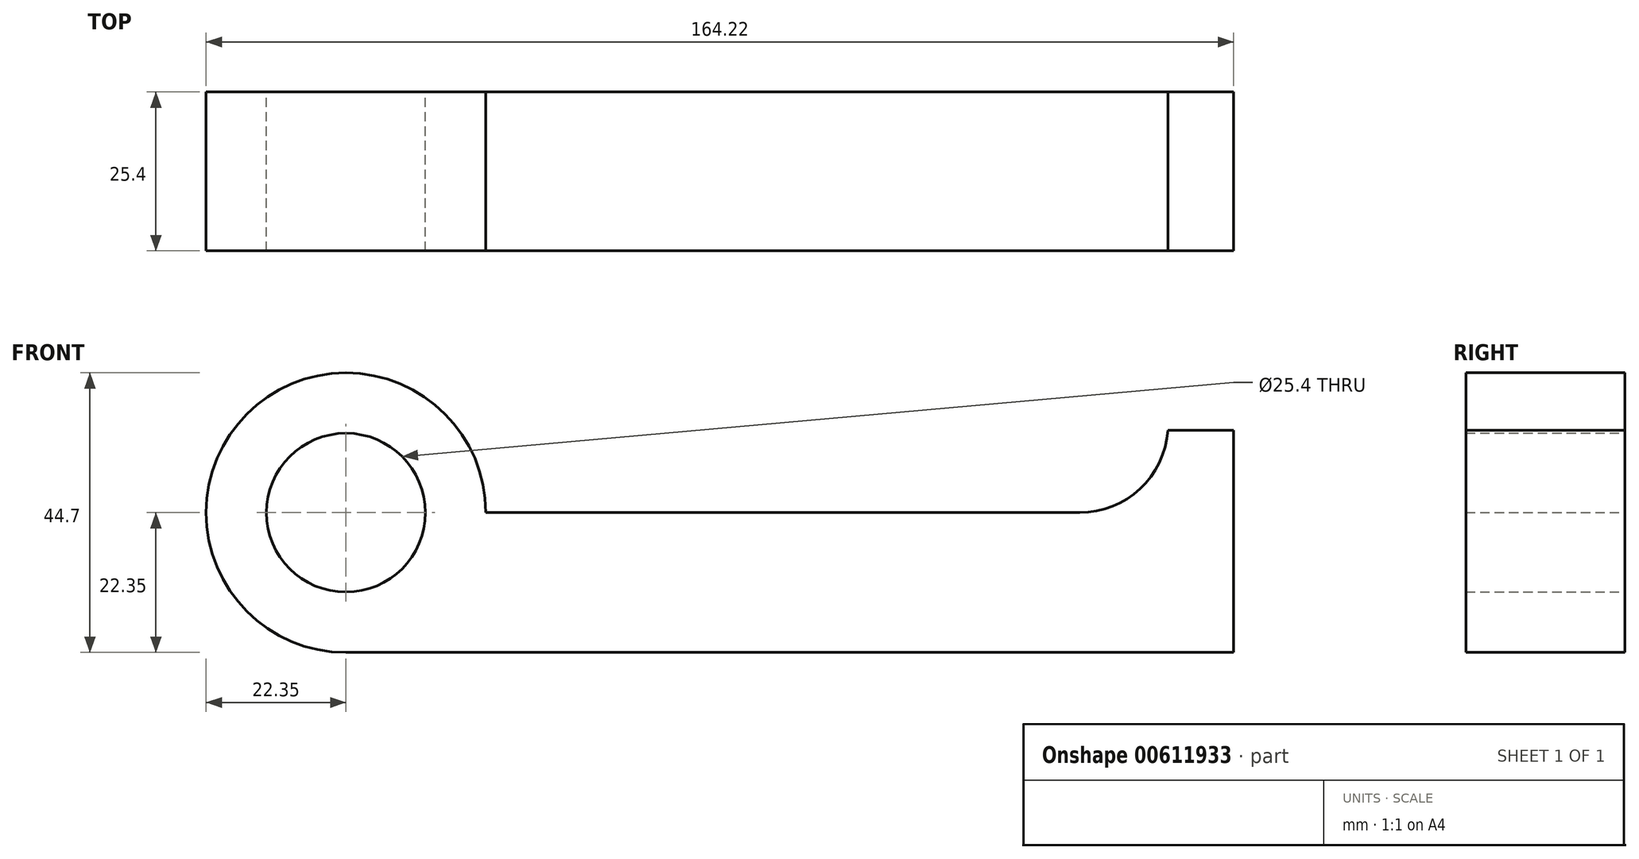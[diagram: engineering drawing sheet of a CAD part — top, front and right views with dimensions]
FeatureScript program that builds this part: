
annotation { "Feature Type Name" : "Feature", "Feature Type Description" : "" }
export const myFeature = defineFeature(function(context is Context, id is Id, definition is map)
    precondition{}
    {
        {
            var Q0;
            Q0=qCreatedBy(makeId("Front.planeOp"),FACE);
            var sketch = newSketch(context, id + "F0", { "sketchPlane" : qUnion([Q0])});
            skCircle(sketch, "E0", {"center": v(0, 0) * mm, "radius": 12.7 * mm});
            skCircle(sketch, "E1", {"center": v(0, 0) * mm, "radius": 22.35 * mm});
            skLineSegment(sketch, "E2", {"start": v(0, -22.35) * mm, "end": v(194.2, -22.35) * mm});
            skLineSegment(sketch, "E3", {"start": v(0, 0) * mm, "end": v(117.25, 0) * mm});
            skArc(sketch, "E4", {"start": v(117.25, 0) * mm, "mid": v(126.9, 3.8) * mm, "end": v(131.36, 13.18) * mm});
            skLineSegment(sketch, "E5", {"start": v(131.36, 13.18) * mm, "end": v(141.87, 13.18) * mm});
            skLineSegment(sketch, "E6", {"start": v(141.87, 13.18) * mm, "end": v(141.87, -22.35) * mm});
            skSolve(sketch);
        }
        {
            var Q0;
            Q0 = qSketchRegion(id + "F0", true);
            extrude(context, id + "F1", {"entities" : qUnion([Q0]), "depth" : 25.4 * mm, "offsetDistance" : 25.4 * mm});
        }
    });
